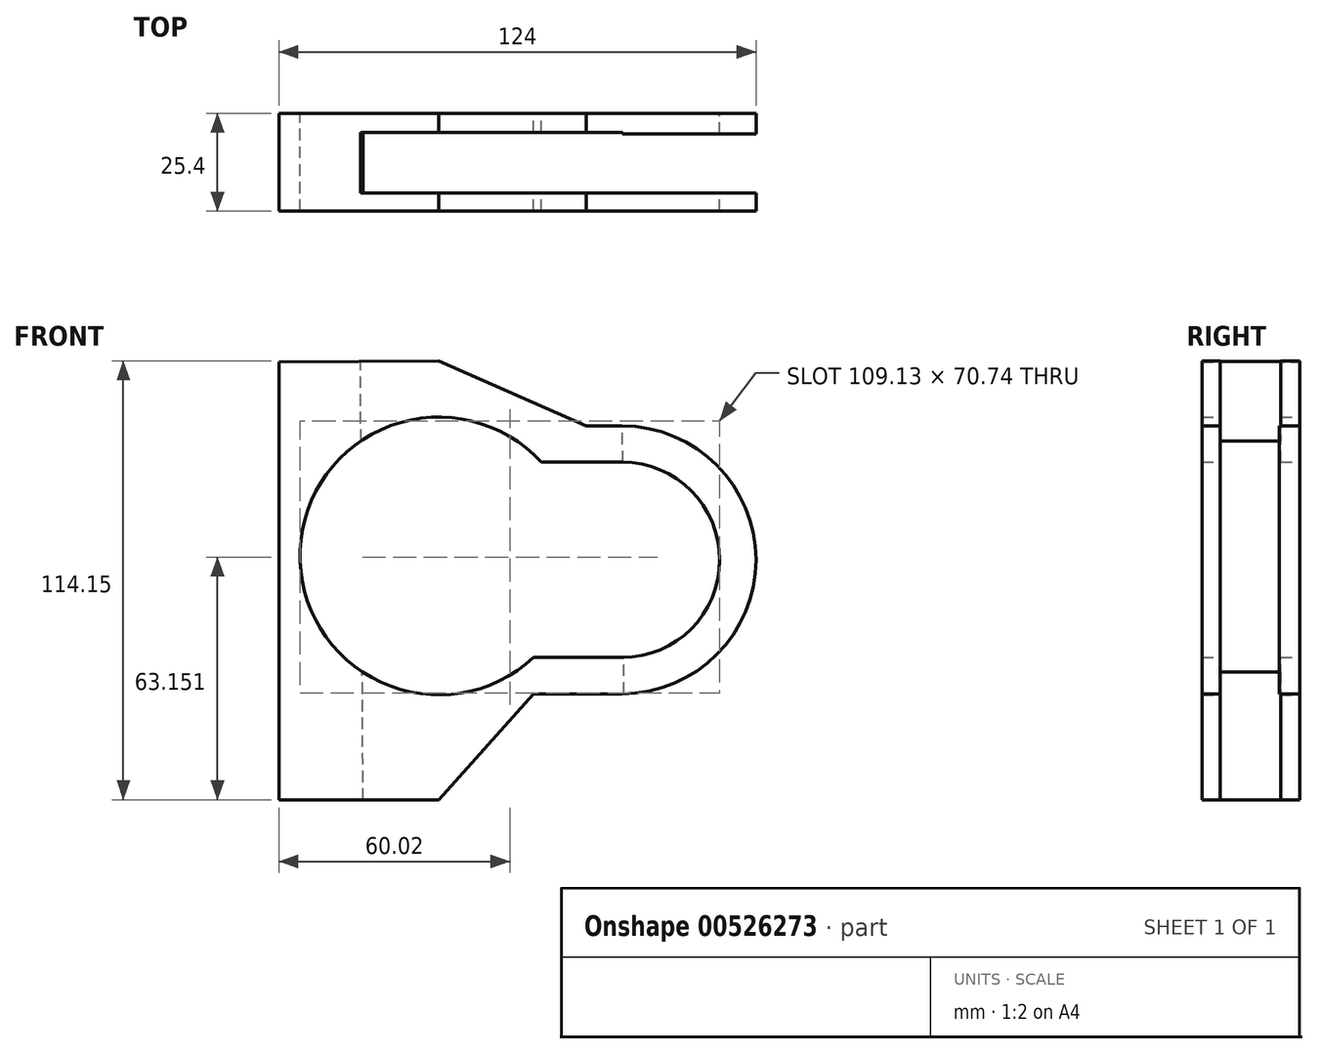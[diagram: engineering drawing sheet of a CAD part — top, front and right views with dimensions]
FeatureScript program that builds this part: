
annotation { "Feature Type Name" : "Feature", "Feature Type Description" : "" }
export const myFeature = defineFeature(function(context is Context, id is Id, definition is map)
    precondition{}
    {
        {
            var Q0;
            Q0=qCreatedBy(makeId("Front.planeOp"),FACE);
            var sketch = newSketch(context, id + "F0", { "sketchPlane" : qUnion([Q0])});
            skLineSegment(sketch, "E0", {"start": v(26.61, 24.41) * mm, "end": v(47.63, 24.41) * mm});
            skArc(sketch, "E1", {"start": v(47.63, -26.41) * mm, "mid": v(73.05, -1) * mm, "end": v(47.63, 24.41) * mm});
            skLineSegment(sketch, "E2", {"start": v(47.63, -26.41) * mm, "end": v(24.63, -26.41) * mm});
            skArc(sketch, "E3", {"start": v(26.61, 24.41) * mm, "mid": v(-36.09, 1.4) * mm, "end": v(24.63, -26.41) * mm});
            skPoint(sketch, "E4.orphan", {"position": v(0, 24.41) * mm});
            skPoint(sketch, "E5.orphan", {"position": v(0, -26.41) * mm});
            skLineSegment(sketch, "E6", {"start": v(24.63, -35.83) * mm, "end": v(47.63, -35.83) * mm});
            skLineSegment(sketch, "E7", {"start": v(24.63, -35.83) * mm, "end": v(0, -63.43) * mm});
            skLineSegment(sketch, "E8", {"start": v(0, -63.43) * mm, "end": v(-41.54, -63.43) * mm});
            skLineSegment(sketch, "E9", {"start": v(-41.54, -63.43) * mm, "end": v(-41.54, 50.47) * mm});
            skLineSegment(sketch, "E10", {"start": v(-41.54, 50.47) * mm, "end": v(0, 50.72) * mm});
            skLineSegment(sketch, "E11", {"start": v(0, 50.72) * mm, "end": v(38.38, 33.83) * mm});
            skLineSegment(sketch, "E12", {"start": v(38.38, 33.83) * mm, "end": v(47.63, 33.83) * mm});
            skArc(sketch, "E13", {"start": v(47.63, 33.83) * mm, "mid": v(82.46, -1) * mm, "end": v(47.63, -35.83) * mm});
            skSolve(sketch);
        }
        {
            var Q0;
            Q0 = qSketchRegion(id + "F0", true);
            extrude(context, id + "F1", {"entities" : qUnion([Q0]), "endBound" : BoundingType.SYMMETRIC, "depth" : 25.4 * mm, "offsetDistance" : 25.4 * mm, "hasSecondDirection" : true, "secondDirectionOppositeDirection" : true, "secondDirectionDepth" : 25.4 * mm});
        }
        {
            var Q0;
            Q0=makeQuery(id+"F1.opExtrude","SWEPT_FACE",FACE,{"disambiguationData":[OSD([sQuery(id+"F0.wireOp",EDGE,"E10")])]});
            var sketch = newSketch(context, id + "F2", { "sketchPlane" : qUnion([Q0])});
            skLineSegment(sketch, "E14.bottom", {"start": v(-20.47, 12.7) * mm, "end": v(47.83, 12.7) * mm});
            skLineSegment(sketch, "E14.top", {"start": v(-20.47, -12.7) * mm, "end": v(47.83, -12.7) * mm});
            skLineSegment(sketch, "E14.left", {"start": v(-20.47, 12.7) * mm, "end": v(-20.47, -12.7) * mm});
            skLineSegment(sketch, "E14.right", {"start": v(47.83, 12.7) * mm, "end": v(47.83, -12.7) * mm});
            skSolve(sketch);
        }
        {
            var Q0;
            Q0 = qSketchRegion(id + "F2", true);
            var sketch = newSketch(context, id + "F3", { "sketchPlane" : qUnion([Q0])});
            skLineSegment(sketch, "E15.bottom", {"start": v(-20.81, 7.37) * mm, "end": v(84.7, 7.37) * mm});
            skLineSegment(sketch, "E15.top", {"start": v(-20.81, -7.94) * mm, "end": v(84.7, -7.94) * mm});
            skLineSegment(sketch, "E15.left", {"start": v(-20.81, 7.37) * mm, "end": v(-20.81, -7.94) * mm});
            skLineSegment(sketch, "E15.right", {"start": v(84.7, 7.37) * mm, "end": v(84.7, -7.94) * mm});
            skSolve(sketch);
        }
        {
            var Q0;
            {var subQ3=sQuery(id+"F2.wireOp",EDGE,"E14.left");Q0=makeQuery(id+"F2.imprint","IMPRINT",FACE,{"disambiguationData":[TD([[makeQuery(id+"F2.imprint","IMPRINT",EDGE,{"derivedFrom":subQ3}),1.0]])]});}
            var sketch = newSketch(context, id + "F4", { "sketchPlane" : qUnion([Q0])});
            skLineSegment(sketch, "E16.bottom", {"start": v(-20.08, 7.74) * mm, "end": v(47.96, 7.74) * mm});
            skLineSegment(sketch, "E16.top", {"start": v(-20.08, -7.95) * mm, "end": v(47.96, -7.95) * mm});
            skLineSegment(sketch, "E16.left", {"start": v(-20.08, 7.74) * mm, "end": v(-20.08, -7.95) * mm});
            skLineSegment(sketch, "E16.right", {"start": v(47.96, 7.74) * mm, "end": v(47.96, -7.95) * mm});
            skSolve(sketch);
        }
        {
            var Q0;
            Q0 = qSketchRegion(id + "F4", true);
            extrude(context, id + "F5", {"entities" : qUnion([Q0]), "operationType" : NewBodyOperationType.REMOVE, "endBound" : BoundingType.THROUGH_ALL, "oppositeDirection" : true, "depth" : 25.4 * mm, "offsetDistance" : 25.4 * mm});
        }
        {
            var Q0;
            {var subQ0=sQuery(id+"F3.wireOp",EDGE,"E15.right");Q0=makeQuery(id+"F3.imprint","IMPRINT",FACE,{"disambiguationData":[TD([[makeQuery(id+"F3.imprint","IMPRINT",EDGE,{"derivedFrom":subQ0}),-1.0]])]});}
            var Q1;
            {var subQ0=sQuery(id+"F3.wireOp",EDGE,"E15.bottom");var subQ1=makeQuery(id+"F2.imprint","IMPRINT",EDGE,{"derivedFrom":sQuery(id+"F2.wireOp",EDGE,"E14.left")});var subQ2=makeQuery(id+"F3.imprint","INTERSECT",VERTEX,{"derivedFrom":[subQ1,subQ0]});Q1=makeQuery(id+"F3.imprint","IMPRINT",FACE,{"disambiguationData":[TD([[makeQuery(id+"F3.imprint","IMPRINT",EDGE,{"disambiguationData":[TD([[subQ2,-1.0]])],"derivedFrom":subQ1}),1.0]])]});}
            var Q2;
            {var subQ0=sQuery(id+"F3.wireOp",EDGE,"E15.bottom");var subQ1=makeQuery(id+"F2.imprint","IMPRINT",EDGE,{"derivedFrom":sQuery(id+"F2.wireOp",EDGE,"E14.right")});var subQ2=makeQuery(id+"F3.imprint","INTERSECT",VERTEX,{"derivedFrom":[subQ1,subQ0]});Q2=makeQuery(id+"F3.imprint","IMPRINT",FACE,{"disambiguationData":[TD([[makeQuery(id+"F3.imprint","IMPRINT",EDGE,{"disambiguationData":[TD([[subQ2,-1.0]])],"derivedFrom":subQ1}),-1.0]])]});}
            extrude(context, id + "F6", {"entities" : qUnion([Q0, Q1, Q2]), "operationType" : NewBodyOperationType.REMOVE, "endBound" : BoundingType.THROUGH_ALL, "oppositeDirection" : true, "depth" : 25.4 * mm, "offsetDistance" : 25.4 * mm});
        }
    });
